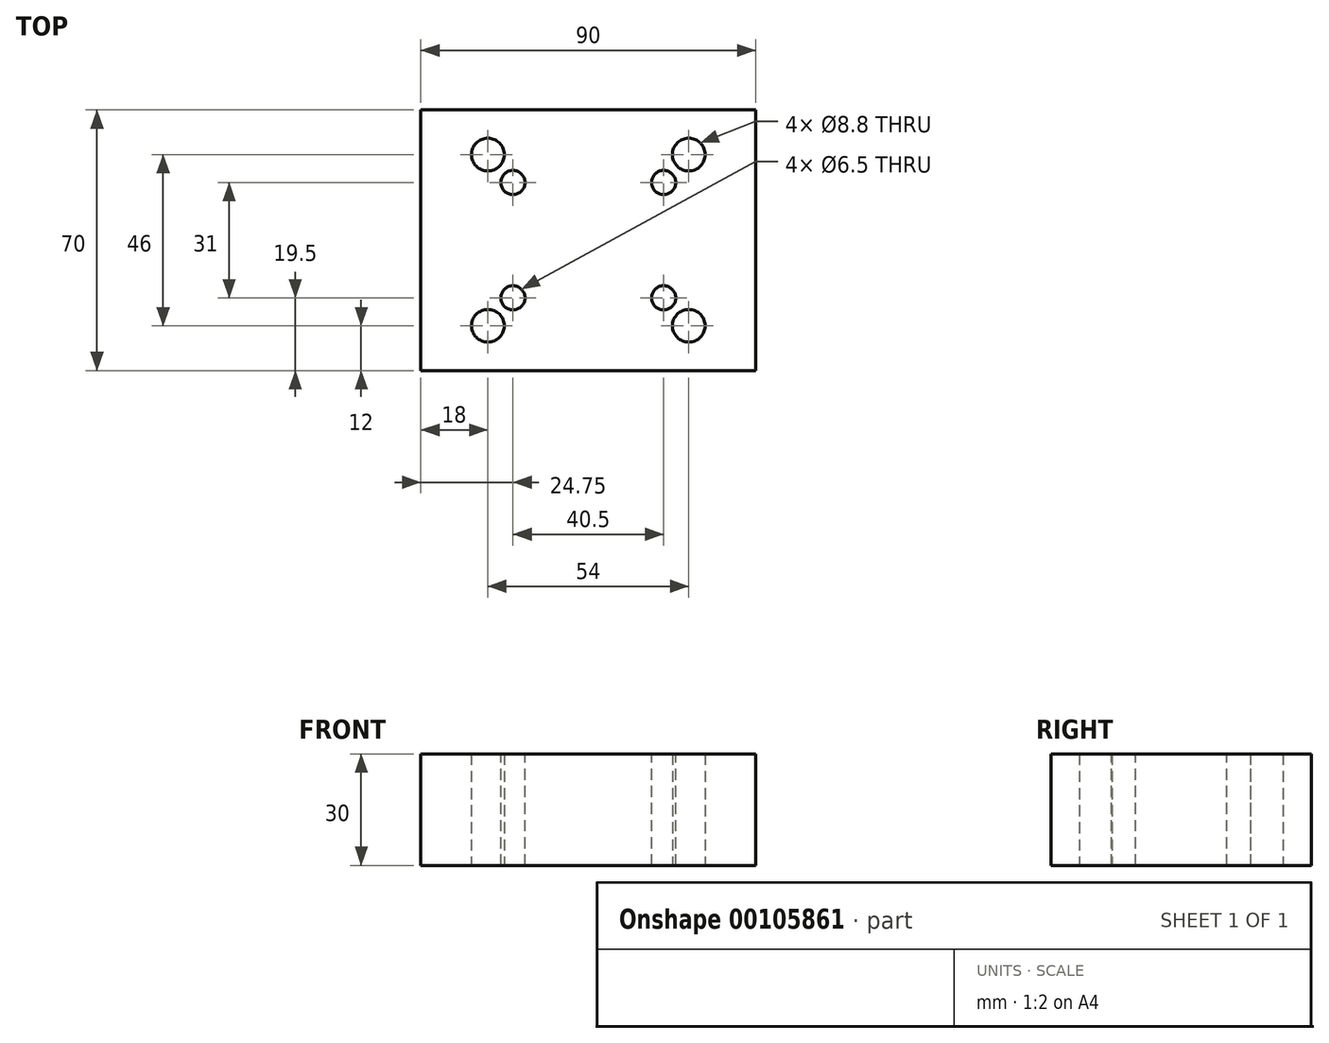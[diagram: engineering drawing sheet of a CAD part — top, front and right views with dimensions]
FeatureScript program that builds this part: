
annotation { "Feature Type Name" : "Feature", "Feature Type Description" : "" }
export const myFeature = defineFeature(function(context is Context, id is Id, definition is map)
    precondition{}
    {
        {
            var Q0;
            Q0=qCreatedBy(makeId("Top.planeOp"),FACE);
            var sketch = newSketch(context, id + "F0", { "sketchPlane" : qUnion([Q0])});
            skLineSegment(sketch, "E0.bottom", {"start": v(-45, -34.19) * mm, "end": v(45, -34.19) * mm});
            skLineSegment(sketch, "E0.top", {"start": v(-45, 35.81) * mm, "end": v(45, 35.81) * mm});
            skLineSegment(sketch, "E0.left", {"start": v(-45, -34.19) * mm, "end": v(-45, 35.81) * mm});
            skLineSegment(sketch, "E0.right", {"start": v(45, -34.19) * mm, "end": v(45, 35.81) * mm});
            skPoint(sketch, "E0.middle", {"position": v(0, 0.81) * mm});
            skPoint(sketch, "E1", {"position": v(-27, 23.81) * mm});
            skPoint(sketch, "E2", {"position": v(-27, -22.19) * mm});
            skPoint(sketch, "E3", {"position": v(27, -22.19) * mm});
            skPoint(sketch, "E4", {"position": v(27, 23.81) * mm});
            skSolve(sketch);
        }
        {
            var Q0;
            Q0 = qSketchRegion(id + "F0", true);
            extrude(context, id + "F1", {"entities" : qUnion([Q0]), "depth" : 30 * mm});
        }
        {
            var Q0;
            Q0=sQuery(id+"F0.wireOp",VERTEX,"E1");
            var Q1;
            Q1=sQuery(id+"F0.wireOp",VERTEX,"E2");
            var Q2;
            Q2=sQuery(id+"F0.wireOp",VERTEX,"E3");
            var Q3;
            Q3=sQuery(id+"F0.wireOp",VERTEX,"E4");
            var Q4;
            Q4=makeQuery(id+"F1.opExtrude","SWEPT_BODY",BODY,{"disambiguationData":[OSD([sQuery(id+"F0.wireOp",EDGE,"E0.bottom"),sQuery(id+"F0.wireOp",EDGE,"E0.top"),sQuery(id+"F0.wireOp",EDGE,"E0.left"),sQuery(id+"F0.wireOp",EDGE,"E0.right")])]});
            hole(context, id + "F2", {"style" : HoleStyle.SIMPLE, "endStyle" : HoleEndStyle.THROUGH, "oppositeDirection" : true, "standardTappedOrClearance" : lookupTablePath({ "standard" : "ISO", "engagement" : "75%", "pitch" : "1.25 mm", "size" : "M10", "type" : "Tapped" }), "standardBlindInLast" : lookupTablePath({ "standard" : "ISO", "engagement" : "75%", "pitch" : "1.25 mm", "size" : "M10", "type" : "Tapped" }), "holeDiameter" : 8.8 * mm, "locations" : qUnion([Q0, Q1, Q2, Q3]), "scope" : qUnion([Q4]), "isTappedThrough" : true, "majorDiameter" : 10 * mm, "showTappedDepth" : true});
        }
        {
            var Q0;
            Q0=makeQuery(id+"F1.opExtrude","CAP_FACE",FACE,{"disambiguationData":[OSD([sQuery(id+"F0.wireOp",EDGE,"E0.bottom"),sQuery(id+"F0.wireOp",EDGE,"E0.top"),sQuery(id+"F0.wireOp",EDGE,"E0.left"),sQuery(id+"F0.wireOp",EDGE,"E0.right")])],"isStart":false});
            var sketch = newSketch(context, id + "F3", { "sketchPlane" : qUnion([Q0])});
            skPoint(sketch, "E5", {"position": v(-20.25, 16.31) * mm});
            skPoint(sketch, "E6", {"position": v(20.25, 16.31) * mm});
            skPoint(sketch, "E7", {"position": v(20.25, -14.69) * mm});
            skPoint(sketch, "E8", {"position": v(-20.25, -14.69) * mm});
            skSolve(sketch);
        }
        {
            var Q0;
            Q0=sQuery(id+"F3.wireOp",VERTEX,"E5");
            var Q1;
            Q1=sQuery(id+"F3.wireOp",VERTEX,"E8");
            var Q2;
            Q2=sQuery(id+"F3.wireOp",VERTEX,"E7");
            var Q3;
            Q3=sQuery(id+"F3.wireOp",VERTEX,"E6");
            var Q4;
            Q4=makeQuery(id+"F1.opExtrude","SWEPT_BODY",BODY,{"disambiguationData":[OSD([sQuery(id+"F0.wireOp",EDGE,"E0.bottom"),sQuery(id+"F0.wireOp",EDGE,"E0.top"),sQuery(id+"F0.wireOp",EDGE,"E0.left"),sQuery(id+"F0.wireOp",EDGE,"E0.right")])]});
            hole(context, id + "F4", {"style" : HoleStyle.SIMPLE, "endStyle" : HoleEndStyle.THROUGH, "holeDiameter" : 6.5 * mm, "locations" : qUnion([Q0, Q1, Q2, Q3]), "scope" : qUnion([Q4]), "isTappedThrough" : true});
        }
    });
